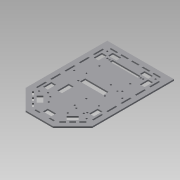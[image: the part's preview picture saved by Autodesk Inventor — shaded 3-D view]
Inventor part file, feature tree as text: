
AUTODESK INVENTOR PART (.ipt)
format: ipt  version: 2015 SP1 (Build 190203100, 203)  size: 326,656 bytes
history: native  units: mm
features: extrude x1, sketch x1
ambient origin geometry x8: Origin, YZ Plane, XZ Plane, XY Plane, X Axis, Y Axis, Z Axis, Center Point
bodies: Body1 (feature_tree)
feature tree (2):
  extrude  "Extrusion2"  Depth=3.0mm
  sketch  "Sketch1"  dims[d0=10.0mm d1=3.0mm d2=20.0mm d4=15.0mm d5=20.0mm d7=15.0mm d10=1.5mm d11=10.0mm d12=3.0mm d13=10.0mm d14=135.0deg d15=45.0deg d16=20.0mm d18=15.0mm d19=20.0mm d21=15.0mm d24=3.0mm d25=20.0mm d26=30.0mm d28=30.0mm d29=30.0mm d31=30.0mm d34=15.0mm d35=3.0mm d36=30.0mm d38=22.5mm d39=30.0mm d41=22.5mm d47=3.0mm d48=0.0mm]
